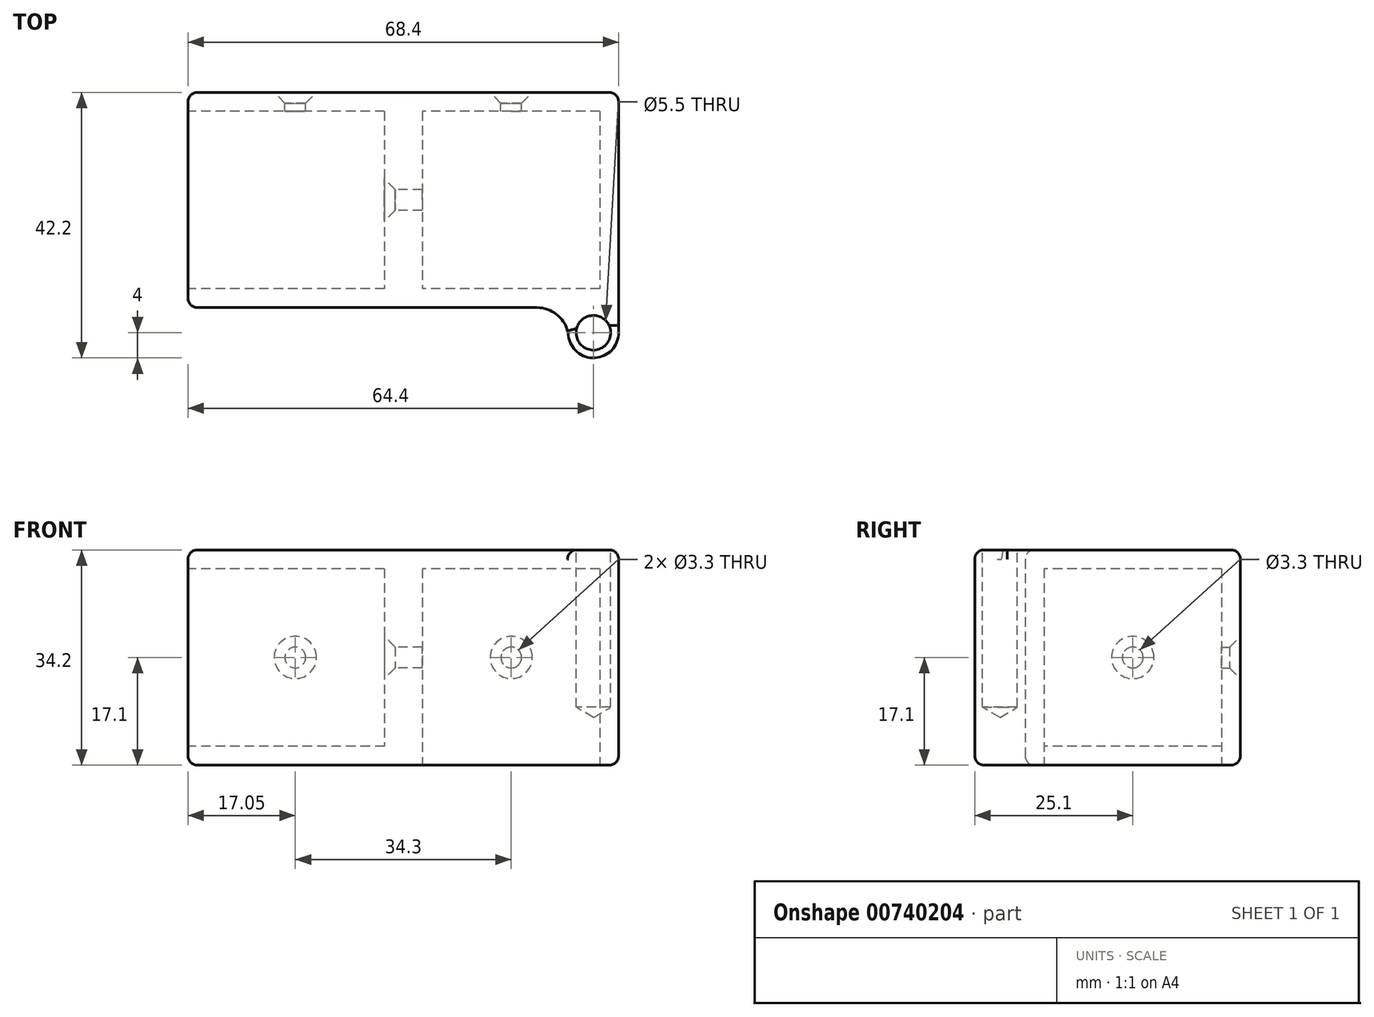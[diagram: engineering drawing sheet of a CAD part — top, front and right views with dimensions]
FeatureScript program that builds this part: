
annotation { "Feature Type Name" : "Feature", "Feature Type Description" : "" }
export const myFeature = defineFeature(function(context is Context, id is Id, definition is map)
    precondition{}
    {
        {
            var Q0;
            Q0=qCreatedBy(makeId("Top.planeOp"),FACE);
            var sketch = newSketch(context, id + "F0", { "sketchPlane" : qUnion([Q0])});
            skLineSegment(sketch, "E0.bottom", {"start": v(-8, 0) * mm, "end": v(-34.2, 0) * mm});
            skLineSegment(sketch, "E0.top", {"start": v(0, 34.2) * mm, "end": v(-34.2, 34.2) * mm});
            skLineSegment(sketch, "E0.left", {"start": v(0, 0) * mm, "end": v(0, 34.2) * mm});
            skLineSegment(sketch, "E0.right", {"start": v(-34.2, 0) * mm, "end": v(-34.2, 34.2) * mm});
            skArc(sketch, "E1", {"start": v(-8, -4) * mm, "mid": v(-4, -8) * mm, "end": v(0, -4) * mm});
            skLineSegment(sketch, "E2", {"start": v(0, 0) * mm, "end": v(0, -4) * mm});
            skLineSegment(sketch, "E3", {"start": v(-8, 0) * mm, "end": v(-8, -4) * mm});
            skLineSegment(sketch, "E4", {"start": v(0, 0) * mm, "end": v(-8, 0) * mm});
            skSolve(sketch);
        }
        {
            var Q0;
            Q0=makeQuery(id+"F0.imprint","IMPRINT",FACE,{"disambiguationData":[TD([[makeQuery(id+"F0.imprint","IMPRINT",EDGE,{"derivedFrom":sQuery(id+"F0.wireOp",EDGE,"E1")}),1.0]])]});
            var Q1;
            Q1=makeQuery(id+"F0.imprint","IMPRINT",FACE,{"disambiguationData":[TD([[makeQuery(id+"F0.imprint","IMPRINT",EDGE,{"derivedFrom":sQuery(id+"F0.wireOp",EDGE,"E0.bottom")}),-1.0]])]});
            extrude(context, id + "F1", {"entities" : qUnion([Q0, Q1]), "depth" : 34.2 * mm, "offsetDistance" : 25 * mm});
        }
        {
            var Q0;
            Q0=makeQuery(id+"F1.opExtrude","SWEPT_FACE",FACE,{"disambiguationData":[OSD([sQuery(id+"F0.wireOp",EDGE,"E0.right")])]});
            var sketch = newSketch(context, id + "F2", { "sketchPlane" : qUnion([Q0])});
            skLineSegment(sketch, "E5.bottom", {"start": v(-34.2, 0) * mm, "end": v(0, 0) * mm});
            skLineSegment(sketch, "E5.top", {"start": v(-34.2, 34.2) * mm, "end": v(0, 34.2) * mm});
            skLineSegment(sketch, "E5.left", {"start": v(-34.2, 0) * mm, "end": v(-34.2, 34.2) * mm});
            skLineSegment(sketch, "E5.right", {"start": v(0, 0) * mm, "end": v(0, 34.2) * mm});
            skSolve(sketch);
        }
        {
            var Q0;
            Q0=qSketchRegion(id+"F2",true);
            extrude(context, id + "F3", {"entities" : qUnion([Q0]), "operationType" : NewBodyOperationType.ADD, "depth" : 34.2 * mm, "offsetDistance" : 25 * mm});
        }
        {
            var Q0;
            Q0=makeQuery(id+"F3.opExtrude","CAP_FACE",FACE,{"disambiguationData":[OSD([sQuery(id+"F2.wireOp",EDGE,"E5.bottom"),sQuery(id+"F2.wireOp",EDGE,"E5.top"),sQuery(id+"F2.wireOp",EDGE,"E5.left"),sQuery(id+"F2.wireOp",EDGE,"E5.right")])],"isStart":false});
            var sketch = newSketch(context, id + "F4", { "sketchPlane" : qUnion([Q0])});
            skLineSegment(sketch, "E6.bottom", {"start": v(-34.2, 34.2) * mm, "end": v(0, 34.2) * mm});
            skLineSegment(sketch, "E6.top", {"start": v(-34.2, 0) * mm, "end": v(0, 0) * mm});
            skLineSegment(sketch, "E6.left", {"start": v(-34.2, 34.2) * mm, "end": v(-34.2, 0) * mm});
            skLineSegment(sketch, "E6.right", {"start": v(0, 34.2) * mm, "end": v(0, 0) * mm});
            skLineSegment(sketch, "E7.0", {"start": v(-31.2, 31.2) * mm, "end": v(-3, 31.2) * mm});
            skLineSegment(sketch, "E7.1", {"start": v(-31.2, 31.2) * mm, "end": v(-31.2, 3) * mm});
            skLineSegment(sketch, "E7.2", {"start": v(-31.2, 3) * mm, "end": v(-3, 3) * mm});
            skLineSegment(sketch, "E7.3", {"start": v(-3, 31.2) * mm, "end": v(-3, 3) * mm});
            skSolve(sketch);
        }
        {
            var Q0;
            Q0=makeQuery(id+"F4.imprint","IMPRINT",FACE,{"disambiguationData":[TD([[makeQuery(id+"F4.imprint","IMPRINT",EDGE,{"derivedFrom":sQuery(id+"F4.wireOp",EDGE,"E7.0")}),-1.0]])]});
            extrude(context, id + "F5", {"entities" : qUnion([Q0]), "operationType" : NewBodyOperationType.REMOVE, "oppositeDirection" : true, "depth" : 31.2 * mm, "offsetDistance" : 25 * mm});
        }
        {
            var Q0;
            Q0=makeQuery(id+"F3.boolean.opBoolean","MERGE",FACE,{"derivedFrom":[makeQuery(id+"F1.opExtrude","SWEPT_FACE",FACE,{"disambiguationData":[OSD([sQuery(id+"F0.wireOp",EDGE,"E0.top")])]}),makeQuery(id+"F3.opExtrude","SWEPT_FACE",FACE,{"disambiguationData":[OSD([sQuery(id+"F2.wireOp",EDGE,"E5.left")])]})]});
            var sketch = newSketch(context, id + "F6", { "sketchPlane" : qUnion([Q0])});
            skPoint(sketch, "E8", {"position": v(17.05, 17.1) * mm});
            skPoint(sketch, "E9", {"position": v(51.35, 17.1) * mm});
            skSolve(sketch);
        }
        {
            var Q0;
            Q0=makeQuery(id+"F5.boolean.opBoolean","COPY",FACE,{"derivedFrom":makeQuery(id+"F5.opExtrude","CAP_FACE",FACE,{"disambiguationData":[OSD([sQuery(id+"F4.wireOp",EDGE,"E7.0"),sQuery(id+"F4.wireOp",EDGE,"E7.1"),sQuery(id+"F4.wireOp",EDGE,"E7.2"),sQuery(id+"F4.wireOp",EDGE,"E7.3")])],"isStart":false})});
            var sketch = newSketch(context, id + "F7", { "sketchPlane" : qUnion([Q0])});
            skPoint(sketch, "E10", {"position": v(-17.1, 17.1) * mm});
            skSolve(sketch);
        }
        {
            var Q0;
            Q0=sQuery(id+"F6.wireOp",VERTEX,"E8");
            var Q1;
            Q1=sQuery(id+"F6.wireOp",VERTEX,"E9");
            var Q2;
            Q2=sQuery(id+"F7.wireOp",VERTEX,"E10");
            var Q3;
            Q3=makeQuery(id+"F1.opExtrude","SWEPT_BODY",BODY,{"disambiguationData":[OSD([sQuery(id+"F0.wireOp",EDGE,"E0.bottom"),sQuery(id+"F0.wireOp",EDGE,"E0.top"),sQuery(id+"F0.wireOp",EDGE,"E0.left"),sQuery(id+"F0.wireOp",EDGE,"E0.right"),sQuery(id+"F0.wireOp",EDGE,"E1"),sQuery(id+"F0.wireOp",EDGE,"6FfksXsB-Y7vq-xAn0-bQFg-GBrETYwM94Cl"),sQuery(id+"F0.wireOp",EDGE,"E2"),sQuery(id+"F0.wireOp",EDGE,"E3")])]});
            hole(context, id + "F8", {"style" : HoleStyle.C_SINK, "endStyle" : HoleEndStyle.BLIND, "standardTappedOrClearance" : lookupTablePath({ "standard" : "ISO", "fit" : "Normal", "size" : "M3", "type" : "Clearance" }), "standardBlindInLast" : lookupTablePath({ "fit" : "Standard", "standard" : "ISO", "size" : "M3", "type" : "Clearance" }), "holeDiameter" : 3.3 * mm, "cSinkDiameter" : 6.72 * mm, "cSinkAngle" : 90 * degree, "majorDiameter" : 5 * mm, "holeDepth" : 25 * mm, "isTappedThrough" : true, "tappedDepth" : 12 * mm, "tapClearance" : 3, "startFromSketch" : true, "locations" : qUnion([Q0, Q1, Q2]), "scope" : qUnion([Q3])});
        }
        {
            var Q0;
            Q0=makeQuery(id+"F3.boolean.opBoolean","MERGE",FACE,{"derivedFrom":[makeQuery(id+"F1.opExtrude","CAP_FACE",FACE,{"disambiguationData":[OSD([sQuery(id+"F0.wireOp",EDGE,"E0.bottom"),sQuery(id+"F0.wireOp",EDGE,"E0.top"),sQuery(id+"F0.wireOp",EDGE,"E0.left"),sQuery(id+"F0.wireOp",EDGE,"E0.right"),sQuery(id+"F0.wireOp",EDGE,"E1"),sQuery(id+"F0.wireOp",EDGE,"E2"),sQuery(id+"F0.wireOp",EDGE,"E3")])],"isStart":false}),makeQuery(id+"F3.opExtrude","SWEPT_FACE",FACE,{"disambiguationData":[OSD([sQuery(id+"F2.wireOp",EDGE,"E5.top")])]})]});
            var sketch = newSketch(context, id + "F9", { "sketchPlane" : qUnion([Q0])});
            skPoint(sketch, "E11", {"position": v(-4, -4) * mm});
            skSolve(sketch);
        }
        {
            var Q0;
            Q0=sQuery(id+"F9.wireOp",VERTEX,"E11");
            var Q1;
            Q1=makeQuery(id+"F1.opExtrude","SWEPT_BODY",BODY,{"disambiguationData":[OSD([sQuery(id+"F0.wireOp",EDGE,"E0.bottom"),sQuery(id+"F0.wireOp",EDGE,"E0.top"),sQuery(id+"F0.wireOp",EDGE,"E0.left"),sQuery(id+"F0.wireOp",EDGE,"E0.right"),sQuery(id+"F0.wireOp",EDGE,"E1"),sQuery(id+"F0.wireOp",EDGE,"E2"),sQuery(id+"F0.wireOp",EDGE,"E3")])]});
            hole(context, id + "F10", {"style" : HoleStyle.SIMPLE, "endStyle" : HoleEndStyle.BLIND, "standardTappedOrClearance" : lookupTablePath({ "standard" : "ISO", "fit" : "Normal", "size" : "M5", "type" : "Clearance" }), "standardBlindInLast" : lookupTablePath({ "fit" : "Standard", "standard" : "ISO", "size" : "M5", "type" : "Clearance" }), "holeDiameter" : 5.5 * mm, "majorDiameter" : 5 * mm, "holeDepth" : 25 * mm, "isTappedThrough" : true, "tappedDepth" : 12 * mm, "tapClearance" : 3, "startFromSketch" : true, "locations" : qUnion([Q0]), "scope" : qUnion([Q1])});
        }
        {
            var Q0;
            Q0=makeQuery(id+"F1.opExtrude","SWEPT_EDGE",EDGE,{"disambiguationData":[OSD([sQuery(id+"F0.wireOp",EDGE,"E0.bottom"),sQuery(id+"F0.wireOp",EDGE,"E3"),sQuery(id+"F0.wireOp",EDGE,"E4")])]});
            fillet(context, id + "F11", {"entities" : qUnion([Q0]), "radius" : 5 * mm, "tangentPropagation" : true, "allowEdgeOverflow" : false});
        }
        {
            var Q0;
            Q0=makeQuery(id+"F3.boolean.opBoolean","MERGE",FACE,{"derivedFrom":[makeQuery(id+"F1.opExtrude","CAP_FACE",FACE,{"disambiguationData":[OSD([sQuery(id+"F0.wireOp",EDGE,"E0.bottom"),sQuery(id+"F0.wireOp",EDGE,"E0.top"),sQuery(id+"F0.wireOp",EDGE,"E0.left"),sQuery(id+"F0.wireOp",EDGE,"E0.right"),sQuery(id+"F0.wireOp",EDGE,"E1"),sQuery(id+"F0.wireOp",EDGE,"E2"),sQuery(id+"F0.wireOp",EDGE,"E3")])],"isStart":true}),makeQuery(id+"F3.opExtrude","SWEPT_FACE",FACE,{"disambiguationData":[OSD([sQuery(id+"F2.wireOp",EDGE,"E5.bottom")])]})]});
            var sketch = newSketch(context, id + "F12", { "sketchPlane" : qUnion([Q0])});
            skLineSegment(sketch, "E12.bottom", {"start": v(0, -34.2) * mm, "end": v(-34.2, -34.2) * mm});
            skLineSegment(sketch, "E12.top", {"start": v(0, 0) * mm, "end": v(-34.2, 0) * mm});
            skLineSegment(sketch, "E12.left", {"start": v(0, -34.2) * mm, "end": v(0, 0) * mm});
            skLineSegment(sketch, "E12.right", {"start": v(-34.2, -34.2) * mm, "end": v(-34.2, 0) * mm});
            skLineSegment(sketch, "E13.0", {"start": v(-31.2, -31.2) * mm, "end": v(-31.2, -3) * mm});
            skLineSegment(sketch, "E13.1", {"start": v(-3, -31.2) * mm, "end": v(-31.2, -31.2) * mm});
            skLineSegment(sketch, "E13.2", {"start": v(-3, -31.2) * mm, "end": v(-3, -3) * mm});
            skLineSegment(sketch, "E13.3", {"start": v(-3, -3) * mm, "end": v(-31.2, -3) * mm});
            skSolve(sketch);
        }
        {
            var Q0;
            Q0=makeQuery(id+"F12.imprint","IMPRINT",FACE,{"disambiguationData":[TD([[makeQuery(id+"F12.imprint","IMPRINT",EDGE,{"derivedFrom":sQuery(id+"F12.wireOp",EDGE,"E13.0")}),-1.0]])]});
            extrude(context, id + "F13", {"entities" : qUnion([Q0]), "operationType" : NewBodyOperationType.REMOVE, "oppositeDirection" : true, "depth" : 31.2 * mm, "offsetDistance" : 25 * mm});
        }
        {
            var Q0;
            Q0=makeQuery(id+"F13.boolean.opBoolean","COPY",EDGE,{"derivedFrom":makeQuery(id+"F13.opExtrude","CAP_EDGE",EDGE,{"disambiguationData":[OSD([sQuery(id+"F12.wireOp",EDGE,"E13.0")])],"isStart":true})});
            var Q1;
            Q1=makeQuery(id+"F13.boolean.opBoolean","COPY",EDGE,{"derivedFrom":makeQuery(id+"F13.opExtrude","CAP_EDGE",EDGE,{"disambiguationData":[OSD([sQuery(id+"F12.wireOp",EDGE,"E13.3")])],"isStart":true})});
            var Q2;
            Q2=makeQuery(id+"F13.boolean.opBoolean","COPY",EDGE,{"derivedFrom":makeQuery(id+"F13.opExtrude","CAP_EDGE",EDGE,{"disambiguationData":[OSD([sQuery(id+"F12.wireOp",EDGE,"E13.2")])],"isStart":true})});
            var Q3;
            Q3=makeQuery(id+"F13.boolean.opBoolean","COPY",EDGE,{"derivedFrom":makeQuery(id+"F13.opExtrude","CAP_EDGE",EDGE,{"disambiguationData":[OSD([sQuery(id+"F12.wireOp",EDGE,"E13.1")])],"isStart":true})});
            var Q4;
            Q4=makeQuery(id+"F3.boolean.opBoolean","MERGE",EDGE,{"derivedFrom":[makeQuery(id+"F1.opExtrude","CAP_EDGE",EDGE,{"disambiguationData":[OSD([sQuery(id+"F0.wireOp",EDGE,"E0.top")])],"isStart":true}),makeQuery(id+"F3.opExtrude","SWEPT_EDGE",EDGE,{"disambiguationData":[OSD([sQuery(id+"F2.wireOp",EDGE,"E5.bottom"),sQuery(id+"F2.wireOp",EDGE,"E5.left")])]})]});
            var Q5;
            Q5=makeQuery(id+"F3.boolean.opBoolean","MERGE",EDGE,{"derivedFrom":[makeQuery(id+"F1.opExtrude","CAP_EDGE",EDGE,{"disambiguationData":[OSD([sQuery(id+"F0.wireOp",EDGE,"E0.bottom")])],"isStart":true}),makeQuery(id+"F3.opExtrude","SWEPT_EDGE",EDGE,{"disambiguationData":[OSD([sQuery(id+"F2.wireOp",EDGE,"E5.bottom"),sQuery(id+"F2.wireOp",EDGE,"E5.right")])]})]});
            var Q6;
            Q6=makeQuery(id+"F1.opExtrude","CAP_EDGE",EDGE,{"disambiguationData":[OSD([sQuery(id+"F0.wireOp",EDGE,"E0.left"),sQuery(id+"F0.wireOp",EDGE,"E2")])],"isStart":true});
            var Q7;
            Q7=makeQuery(id+"F3.opExtrude","CAP_EDGE",EDGE,{"disambiguationData":[OSD([sQuery(id+"F2.wireOp",EDGE,"E5.bottom")])],"isStart":false});
            var Q8;
            Q8=makeQuery(id+"F3.opExtrude","CAP_EDGE",EDGE,{"disambiguationData":[OSD([sQuery(id+"F2.wireOp",EDGE,"E5.right")])],"isStart":false});
            var Q9;
            Q9=makeQuery(id+"F3.opExtrude","CAP_EDGE",EDGE,{"disambiguationData":[OSD([sQuery(id+"F2.wireOp",EDGE,"E5.top")])],"isStart":false});
            var Q10;
            Q10=makeQuery(id+"F3.opExtrude","CAP_EDGE",EDGE,{"disambiguationData":[OSD([sQuery(id+"F2.wireOp",EDGE,"E5.left")])],"isStart":false});
            var Q11;
            Q11=makeQuery(id+"F5.boolean.opBoolean","COPY",EDGE,{"derivedFrom":makeQuery(id+"F5.opExtrude","CAP_EDGE",EDGE,{"disambiguationData":[OSD([sQuery(id+"F4.wireOp",EDGE,"E7.0")])],"isStart":true})});
            var Q12;
            Q12=makeQuery(id+"F5.boolean.opBoolean","COPY",EDGE,{"derivedFrom":makeQuery(id+"F5.opExtrude","CAP_EDGE",EDGE,{"disambiguationData":[OSD([sQuery(id+"F4.wireOp",EDGE,"E7.3")])],"isStart":true})});
            var Q13;
            Q13=makeQuery(id+"F5.boolean.opBoolean","COPY",EDGE,{"derivedFrom":makeQuery(id+"F5.opExtrude","CAP_EDGE",EDGE,{"disambiguationData":[OSD([sQuery(id+"F4.wireOp",EDGE,"E7.2")])],"isStart":true})});
            var Q14;
            Q14=makeQuery(id+"F5.boolean.opBoolean","COPY",EDGE,{"derivedFrom":makeQuery(id+"F5.opExtrude","CAP_EDGE",EDGE,{"disambiguationData":[OSD([sQuery(id+"F4.wireOp",EDGE,"E7.1")])],"isStart":true})});
            var Q15;
            Q15=makeQuery(id+"F3.boolean.opBoolean","MERGE",EDGE,{"derivedFrom":[makeQuery(id+"F1.opExtrude","CAP_EDGE",EDGE,{"disambiguationData":[OSD([sQuery(id+"F0.wireOp",EDGE,"E0.bottom")])],"isStart":false}),makeQuery(id+"F3.opExtrude","SWEPT_EDGE",EDGE,{"disambiguationData":[OSD([sQuery(id+"F2.wireOp",EDGE,"E5.top"),sQuery(id+"F2.wireOp",EDGE,"E5.right")])]})]});
            var Q16;
            Q16=makeQuery(id+"F3.boolean.opBoolean","MERGE",EDGE,{"derivedFrom":[makeQuery(id+"F1.opExtrude","CAP_EDGE",EDGE,{"disambiguationData":[OSD([sQuery(id+"F0.wireOp",EDGE,"E0.top")])],"isStart":false}),makeQuery(id+"F3.opExtrude","SWEPT_EDGE",EDGE,{"disambiguationData":[OSD([sQuery(id+"F2.wireOp",EDGE,"E5.top"),sQuery(id+"F2.wireOp",EDGE,"E5.left")])]})]});
            var Q17;
            Q17=makeQuery(id+"F1.opExtrude","CAP_EDGE",EDGE,{"disambiguationData":[OSD([sQuery(id+"F0.wireOp",EDGE,"E0.left"),sQuery(id+"F0.wireOp",EDGE,"E2")])],"isStart":false});
            var Q18;
            Q18=makeQuery(id+"F1.opExtrude","SWEPT_EDGE",EDGE,{"disambiguationData":[OSD([sQuery(id+"F0.wireOp",EDGE,"E0.top"),sQuery(id+"F0.wireOp",EDGE,"E0.left")])]});
            fillet(context, id + "F14", {"entities" : qUnion([Q0, Q1, Q2, Q3, Q4, Q5, Q6, Q7, Q8, Q9, Q10, Q11, Q12, Q13, Q14, Q15, Q16, Q17, Q18]), "radius" : 1.5 * mm, "tangentPropagation" : true, "allowEdgeOverflow" : false});
        }
    });
